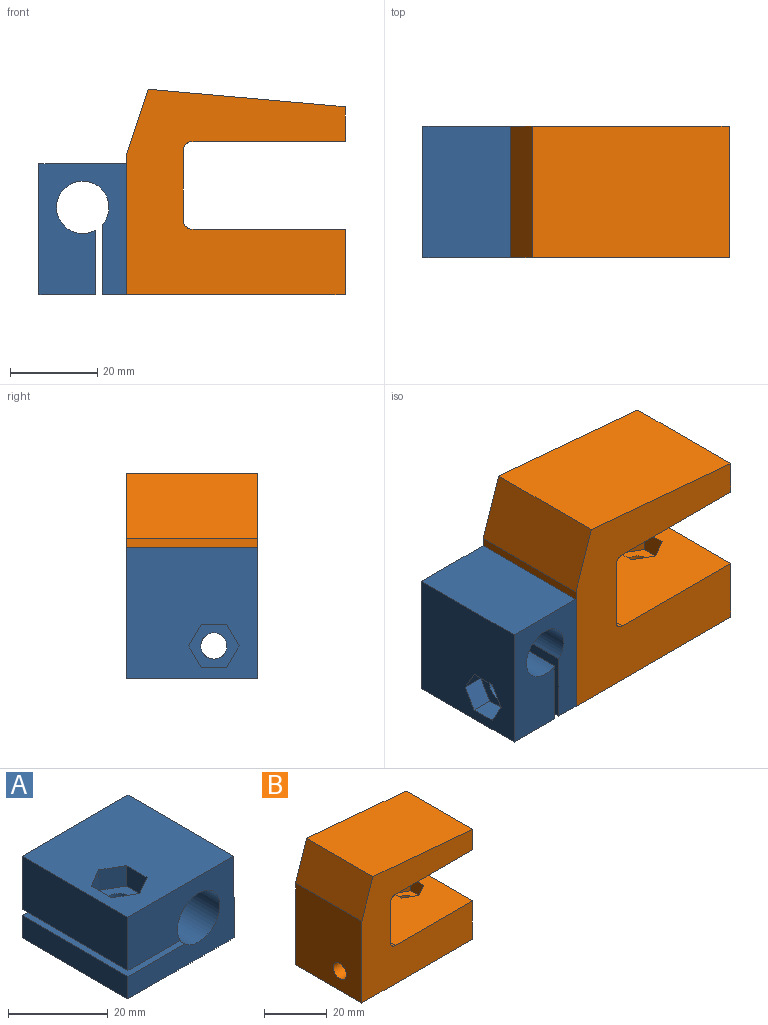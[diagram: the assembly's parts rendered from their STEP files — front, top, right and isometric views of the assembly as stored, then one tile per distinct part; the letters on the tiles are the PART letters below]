
ASSEMBLY  parts=2 mates=1
PART A: 19 faces, bbox 30x30x20 mm
  f0: plane 30x30mm, normal (0,0,1), area 813.4mm2, adj f7,f8,f9,f10,f12,f13,f14,f15
  f1: cylinder r=3mm len=8mm, axis (0,0,1), area 150.8mm2, adj f2,f18
  f2: plane 30x14.8mm, normal (0,0,-1), area 415.8mm2, adj f1,f3,f8,f9,f10
  f3: cylinder r=6mm len=30mm, axis (0,1,0), area 1072.6mm2, adj f2,f4,f9,f10
  f4: plane 30x16.03mm, normal (0,0,1), area 452.7mm2, adj f3,f5,f9,f10,f11
  f5: plane 30x5.5mm, normal (-1,0,0), area 165mm2, adj f4,f6,f9,f10
  f6: plane 30x30mm, normal (0,0,-1), area 871.7mm2, adj f5,f7,f9,f10,f11
  f7: plane 30x20mm, normal (1,0,0), area 600mm2, adj f0,f6,f9,f10
  f8: plane 30x13mm, normal (-1,0,0), area 390mm2, adj f0,f2,f9,f10
  f9: plane 30x20mm, normal (0,-1,0), area 463.9mm2, adj f0,f2,f3,f4,f5,f6,f7,f8
  f10: plane 30x20mm, normal (0,1,0), area 463.9mm2, adj f0,f2,f3,f4,f5,f6,f7,f8
  f11: cylinder r=3mm len=6mm, axis (0,0,1), area 103.7mm2, adj f4,f6
  f12: plane 5x5mm, normal (-0.5,0.87,0), area 28.9mm2, adj f0,f13,f17,f18
  f13: plane 5.77x5mm, normal (-1,0,0), area 28.9mm2, adj f0,f12,f14,f18
  f14: plane 5x5mm, normal (-0.5,-0.87,0), area 28.9mm2, adj f0,f13,f15,f18
  f15: plane 5x5mm, normal (0.5,-0.87,0), area 28.9mm2, adj f0,f14,f16,f18
  f16: plane 5.77x5mm, normal (1,0,0), area 28.9mm2, adj f0,f15,f17,f18
  f17: plane 5x5mm, normal (0.5,0.87,0), area 28.9mm2, adj f0,f12,f16,f18
  f18: plane 11.55x10mm, normal (0,0,1), area 58.3mm2, adj f1,f12,f13,f14,f15,f16,f17
PART B: 22 faces, bbox 50x30x47 mm
  f0: plane 35x30mm, normal (0,0,1), area 963.4mm2, adj f4,f5,f11,f12,f13,f14,f15,f16
  f1: plane 30x15mm, normal (-0.95,0,0.32), area 474.3mm2, adj f2,f10,f11,f12
  f2: plane 32x30mm, normal (-1,0,0), area 931.7mm2, adj f1,f3,f11,f12,f21
  f3: plane 50x30mm, normal (0,0,-1), area 1471.7mm2, adj f2,f4,f11,f12,f20
  f4: plane 30x15mm, normal (1,0,0), area 421.7mm2, adj f0,f3,f11,f12,f21
  f5: cylinder r=2mm len=30mm, axis (0,1,0), area 94.2mm2, adj f0,f6,f11,f12
  f6: plane 30x16mm, normal (1,0,0), area 480mm2, adj f5,f7,f11,f12
  f7: cylinder r=2mm len=30mm, axis (0,1,0), area 94.2mm2, adj f6,f8,f11,f12
  f8: plane 35x30mm, normal (0,0,-1), area 1050mm2, adj f7,f9,f11,f12
  f9: plane 30x8mm, normal (1,0,0), area 240mm2, adj f8,f10,f11,f12
  f10: plane 45x30mm, normal (0.09,0,1), area 1355.3mm2, adj f1,f9,f11,f12
  f11: plane 50x47mm, normal (0,-1,0), area 1484.2mm2, adj f0,f1,f2,f3,f4,f5,f6,f7
  f12: plane 50x47mm, normal (0,1,0), area 1484.2mm2, adj f0,f1,f2,f3,f4,f5,f6,f7
  f13: plane 5x5mm, normal (-0.5,0.87,0), area 28.9mm2, adj f0,f14,f18,f19
  f14: plane 5.77x5mm, normal (-1,0,0), area 28.9mm2, adj f0,f13,f15,f19
  f15: plane 5x5mm, normal (-0.5,-0.87,0), area 28.9mm2, adj f0,f14,f16,f19
  f16: plane 5x5mm, normal (0.5,-0.87,0), area 28.9mm2, adj f0,f15,f17,f19
  f17: plane 5.77x5mm, normal (1,0,0), area 28.9mm2, adj f0,f16,f18,f19
  f18: plane 5x5mm, normal (0.5,0.87,0), area 28.9mm2, adj f0,f13,f17,f19
  f19: plane 11.55x10mm, normal (0,0,1), area 58.3mm2, adj f13,f14,f15,f16,f17,f18,f20
  f20: cylinder r=3mm len=10mm, axis (0,0,1), area 188.5mm2, adj f3,f19
  f21: cylinder r=3mm len=50mm, axis (-1,0,0), area 942.5mm2, adj f2,f4
PLACE A rot(axis=(0,-1,0),90deg) t=(-32.95,-44.56,24.19)mm
PLACE B rot(axis=(0,1,0),0deg) t=(-12.95,-44.56,-5.81)mm
MATE cylindrical B.f21 <-> A.f1  axis (-1,0,0) through (-12.95,-64.56,1.69)mm
